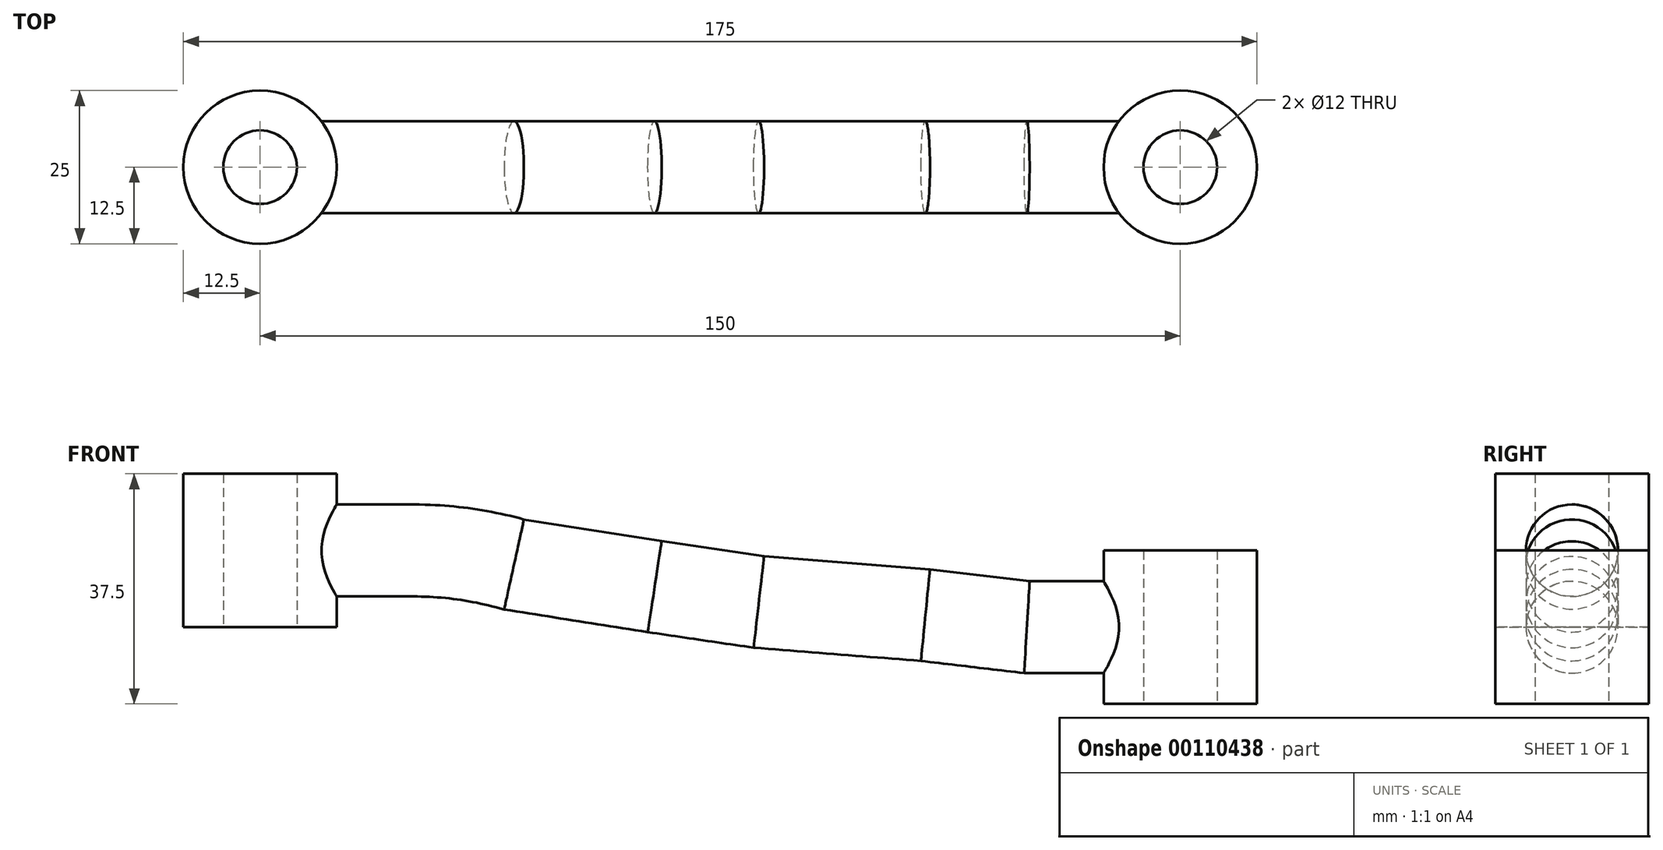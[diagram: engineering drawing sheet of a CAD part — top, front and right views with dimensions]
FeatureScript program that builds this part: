
annotation { "Feature Type Name" : "Feature", "Feature Type Description" : "" }
export const myFeature = defineFeature(function(context is Context, id is Id, definition is map)
    precondition{}
    {
        {
            var Q0;
            Q0=qCreatedBy(makeId("Top.planeOp"),FACE);
            var sketch = newSketch(context, id + "F0", { "sketchPlane" : qUnion([Q0])});
            skCircle(sketch, "E0", {"center": v(0, 0) * mm, "radius": 12.5 * mm});
            skCircle(sketch, "E1", {"center": v(0, 0) * mm, "radius": 6 * mm});
            skSolve(sketch);
        }
        {
            var Q0;
            Q0=makeQuery(id+"F0.imprint","IMPRINT",FACE,{"disambiguationData":[TD([[makeQuery(id+"F0.imprint","IMPRINT",EDGE,{"derivedFrom":sQuery(id+"F0.wireOp",EDGE,"E0")}),1.0]])]});
            var Q1;
            Q1=makeQuery(id+"F0.imprint","IMPRINT",FACE,{"disambiguationData":[TD([[makeQuery(id+"F0.imprint","IMPRINT",EDGE,{"derivedFrom":sQuery(id+"F0.wireOp",EDGE,"yvNvso5l-pkXu-Uv1k-z5F3-GiXRFfFFZvvc")}),1.0]])]});
            extrude(context, id + "F1", {"entities" : qUnion([Q0, Q1]), "depth" : 25 * mm});
        }
        {
            var Q0;
            Q0=qCreatedBy(makeId("Front.planeOp"),FACE);
            var sketch = newSketch(context, id + "F2", { "sketchPlane" : qUnion([Q0])});
            skLineSegment(sketch, "E2", {"start": v(0, 12.5) * mm, "end": v(25, 12.5) * mm});
            skLineSegment(sketch, "E3", {"start": v(125, 0) * mm, "end": v(150, 0) * mm});
            skLineSegment(sketch, "E4", {"start": v(0, 0) * mm, "end": v(0, 25) * mm, "construction": true});
            skArc(sketch, "E5", {"start": v(41.4, 10.22) * mm, "mid": v(33.28, 11.93) * mm, "end": v(25, 12.5) * mm});
            skLineSegment(sketch, "E6", {"start": v(41.4, 10.22) * mm, "end": v(64.33, 6.6) * mm});
            skLineSegment(sketch, "E7", {"start": v(64.33, 6.6) * mm, "end": v(81.3, 4.1) * mm});
            skLineSegment(sketch, "E8", {"start": v(81.3, 4.1) * mm, "end": v(108.46, 1.96) * mm});
            skLineSegment(sketch, "E9", {"start": v(108.46, 1.96) * mm, "end": v(125, 0) * mm});
            skSolve(sketch);
        }
        {
            var Q0;
            Q0=qCreatedBy(makeId("Top.planeOp"),FACE);
            var sketch = newSketch(context, id + "F3", { "sketchPlane" : qUnion([Q0])});
            skCircle(sketch, "E10", {"center": v(150, 0) * mm, "radius": 12.5 * mm});
            skCircle(sketch, "E11", {"center": v(150, 0) * mm, "radius": 6 * mm});
            skSolve(sketch);
        }
        {
            var Q0;
            Q0=makeQuery(id+"F3.imprint","IMPRINT",FACE,{"disambiguationData":[TD([[makeQuery(id+"F3.imprint","IMPRINT",EDGE,{"derivedFrom":sQuery(id+"F3.wireOp",EDGE,"E10")}),1.0]])]});
            extrude(context, id + "F4", {"entities" : qUnion([Q0]), "endBound" : BoundingType.SYMMETRIC, "depth" : 25 * mm});
        }
        {
            var Q0;
            Q0=qCreatedBy(makeId("Right.planeOp"),FACE);
            var sketch = newSketch(context, id + "F5", { "sketchPlane" : qUnion([Q0])});
            skCircle(sketch, "E12", {"center": v(0, 12.5) * mm, "radius": 7.5 * mm});
            skSolve(sketch);
        }
        {
            var Q0;
            Q0 = qSketchRegion(id + "F5", true);
            var Q1;
            Q1 = qConstructionFilter(qBodyType(qCreatedBy(id + "F2" ,EDGE), BodyType.WIRE), ConstructionObject.NO);
            sweep(context, id + "F6", {"operationType" : NewBodyOperationType.ADD, "profiles" : qUnion([Q0]), "path" : qUnion([Q1])});
        }
        {
            var Q0;
            Q0=qCreatedBy(makeId("Top.planeOp"),FACE);
            var sketch = newSketch(context, id + "F7", { "sketchPlane" : qUnion([Q0])});
            skCircle(sketch, "E13", {"center": v(0, 0) * mm, "radius": 6 * mm});
            skSolve(sketch);
        }
        {
            var Q0;
            Q0=makeQuery(id+"F7.imprint","IMPRINT",FACE,{"disambiguationData":[TD([[makeQuery(id+"F7.imprint","IMPRINT",EDGE,{"derivedFrom":sQuery(id+"F7.wireOp",EDGE,"E13")}),1.0]])]});
            extrude(context, id + "F8", {"entities" : qUnion([Q0]), "operationType" : NewBodyOperationType.REMOVE, "depth" : 25 * mm});
        }
        {
            var Q0;
            Q0=makeQuery(id+"F4.opExtrude","CAP_FACE",FACE,{"disambiguationData":[OSD([sQuery(id+"F3.wireOp",EDGE,"E10"),sQuery(id+"F3.wireOp",EDGE,"E11")])],"isStart":false});
            var sketch = newSketch(context, id + "F9", { "sketchPlane" : qUnion([Q0])});
            skCircle(sketch, "E14", {"center": v(150, 0) * mm, "radius": 6 * mm});
            skSolve(sketch);
        }
        {
            var Q0;
            Q0=makeQuery(id+"F9.imprint","IMPRINT",FACE,{"disambiguationData":[TD([[makeQuery(id+"F9.imprint","IMPRINT",EDGE,{"derivedFrom":sQuery(id+"F9.wireOp",EDGE,"E14")}),1.0]])]});
            extrude(context, id + "F10", {"entities" : qUnion([Q0]), "operationType" : NewBodyOperationType.REMOVE, "oppositeDirection" : true, "depth" : 25 * mm});
        }
    });
